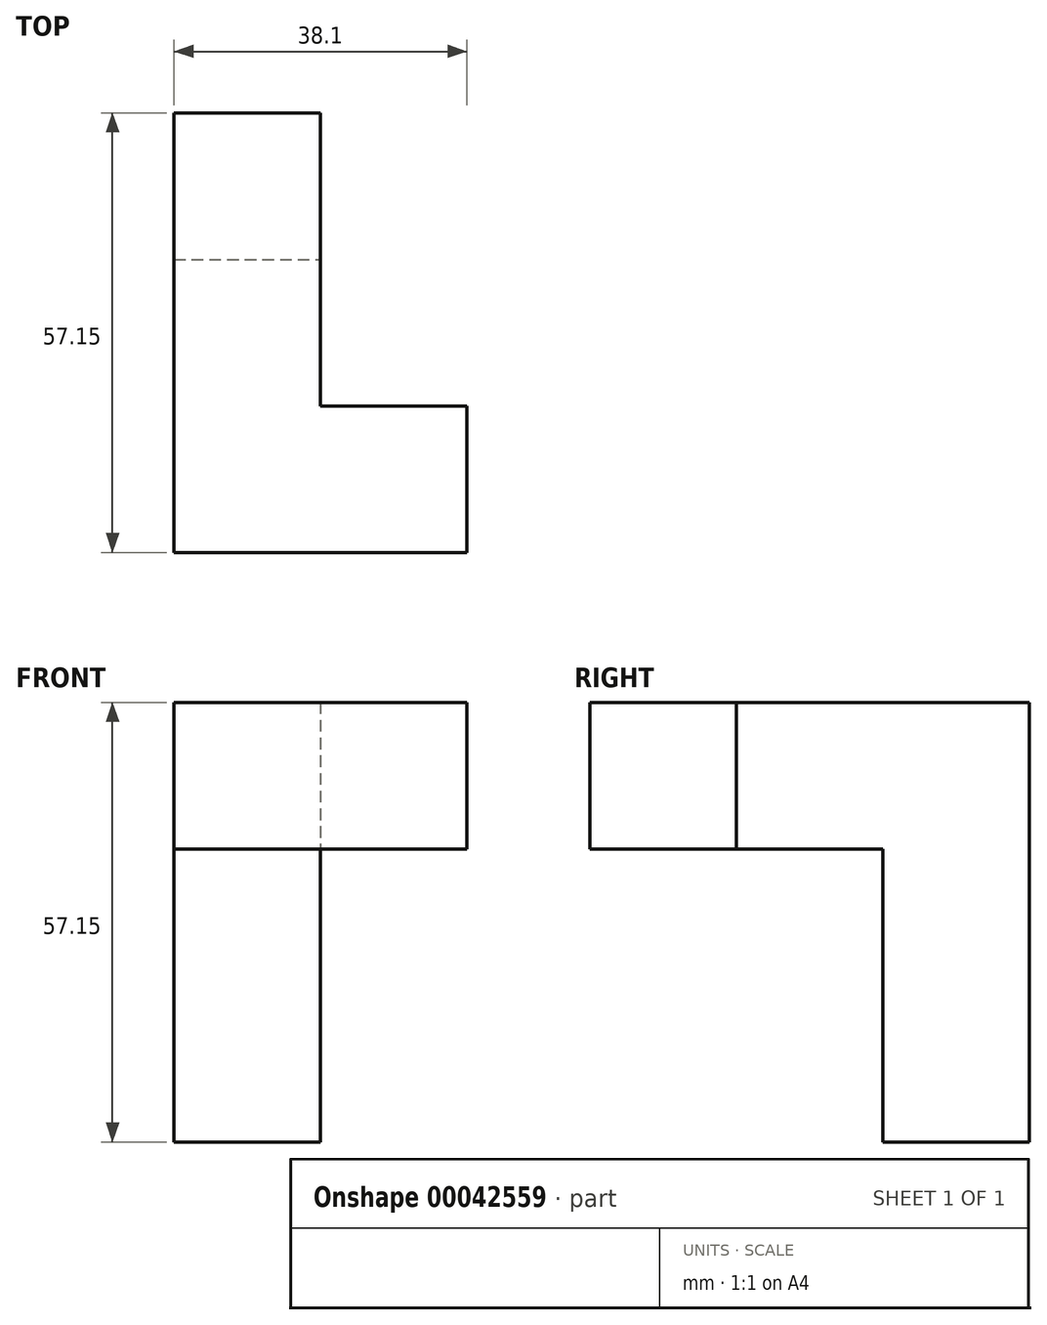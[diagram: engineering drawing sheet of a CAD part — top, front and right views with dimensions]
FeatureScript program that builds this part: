
annotation { "Feature Type Name" : "Feature", "Feature Type Description" : "" }
export const myFeature = defineFeature(function(context is Context, id is Id, definition is map)
    precondition{}
    {
        {
            var Q0;
            Q0=qCreatedBy(makeId("Front.planeOp"),FACE);
            var sketch = newSketch(context, id + "F0", { "sketchPlane" : qUnion([Q0])});
            skLineSegment(sketch, "E0.bottom", {"start": v(0, 0) * mm, "end": v(19.05, 0) * mm});
            skLineSegment(sketch, "E0.top", {"start": v(0, 57.15) * mm, "end": v(19.05, 57.15) * mm});
            skLineSegment(sketch, "E0.left", {"start": v(0, 0) * mm, "end": v(0, 57.15) * mm});
            skLineSegment(sketch, "E0.right", {"start": v(19.05, 0) * mm, "end": v(19.05, 57.15) * mm});
            skSolve(sketch);
        }
        {
            var Q0;
            Q0=qSketchRegion(id+"F0",true);
            extrude(context, id + "F1", {"entities" : qUnion([Q0]), "depth" : 19.05 * mm});
        }
        {
            var Q0;
            Q0=makeQuery(id+"F1.opExtrude","CAP_FACE",FACE,{"disambiguationData":[OSD([sQuery(id+"F0.wireOp",EDGE,"E0.bottom"),sQuery(id+"F0.wireOp",EDGE,"E0.top"),sQuery(id+"F0.wireOp",EDGE,"E0.left"),sQuery(id+"F0.wireOp",EDGE,"E0.right")])],"isStart":false});
            var sketch = newSketch(context, id + "F2", { "sketchPlane" : qUnion([Q0])});
            skLineSegment(sketch, "E1.bottom", {"start": v(0, 57.15) * mm, "end": v(19.05, 57.15) * mm});
            skLineSegment(sketch, "E1.top", {"start": v(0, 38.1) * mm, "end": v(19.05, 38.1) * mm});
            skLineSegment(sketch, "E1.left", {"start": v(0, 57.15) * mm, "end": v(0, 38.1) * mm});
            skLineSegment(sketch, "E1.right", {"start": v(19.05, 57.15) * mm, "end": v(19.05, 38.1) * mm});
            skSolve(sketch);
        }
        {
            var Q0;
            Q0=qSketchRegion(id+"F2",true);
            extrude(context, id + "F3", {"entities" : qUnion([Q0]), "operationType" : NewBodyOperationType.ADD, "depth" : 38.1 * mm});
        }
        {
            var Q0;
            Q0=makeQuery(id+"F3.boolean.opBoolean","MERGE",FACE,{"derivedFrom":[makeQuery(id+"F1.opExtrude","SWEPT_FACE",FACE,{"disambiguationData":[OSD([sQuery(id+"F0.wireOp",EDGE,"E0.right")])]}),makeQuery(id+"F3.opExtrude","SWEPT_FACE",FACE,{"disambiguationData":[OSD([sQuery(id+"F2.wireOp",EDGE,"E1.right")])]})]});
            var sketch = newSketch(context, id + "F4", { "sketchPlane" : qUnion([Q0])});
            skLineSegment(sketch, "E2.bottom", {"start": v(-57.15, 57.15) * mm, "end": v(-38.1, 57.15) * mm});
            skLineSegment(sketch, "E2.top", {"start": v(-57.15, 38.1) * mm, "end": v(-38.1, 38.1) * mm});
            skLineSegment(sketch, "E2.left", {"start": v(-57.15, 57.15) * mm, "end": v(-57.15, 38.1) * mm});
            skLineSegment(sketch, "E2.right", {"start": v(-38.1, 57.15) * mm, "end": v(-38.1, 38.1) * mm});
            skSolve(sketch);
        }
        {
            var Q0;
            Q0=qSketchRegion(id+"F4",true);
            extrude(context, id + "F5", {"entities" : qUnion([Q0]), "operationType" : NewBodyOperationType.ADD, "depth" : 19.05 * mm});
        }
    });
